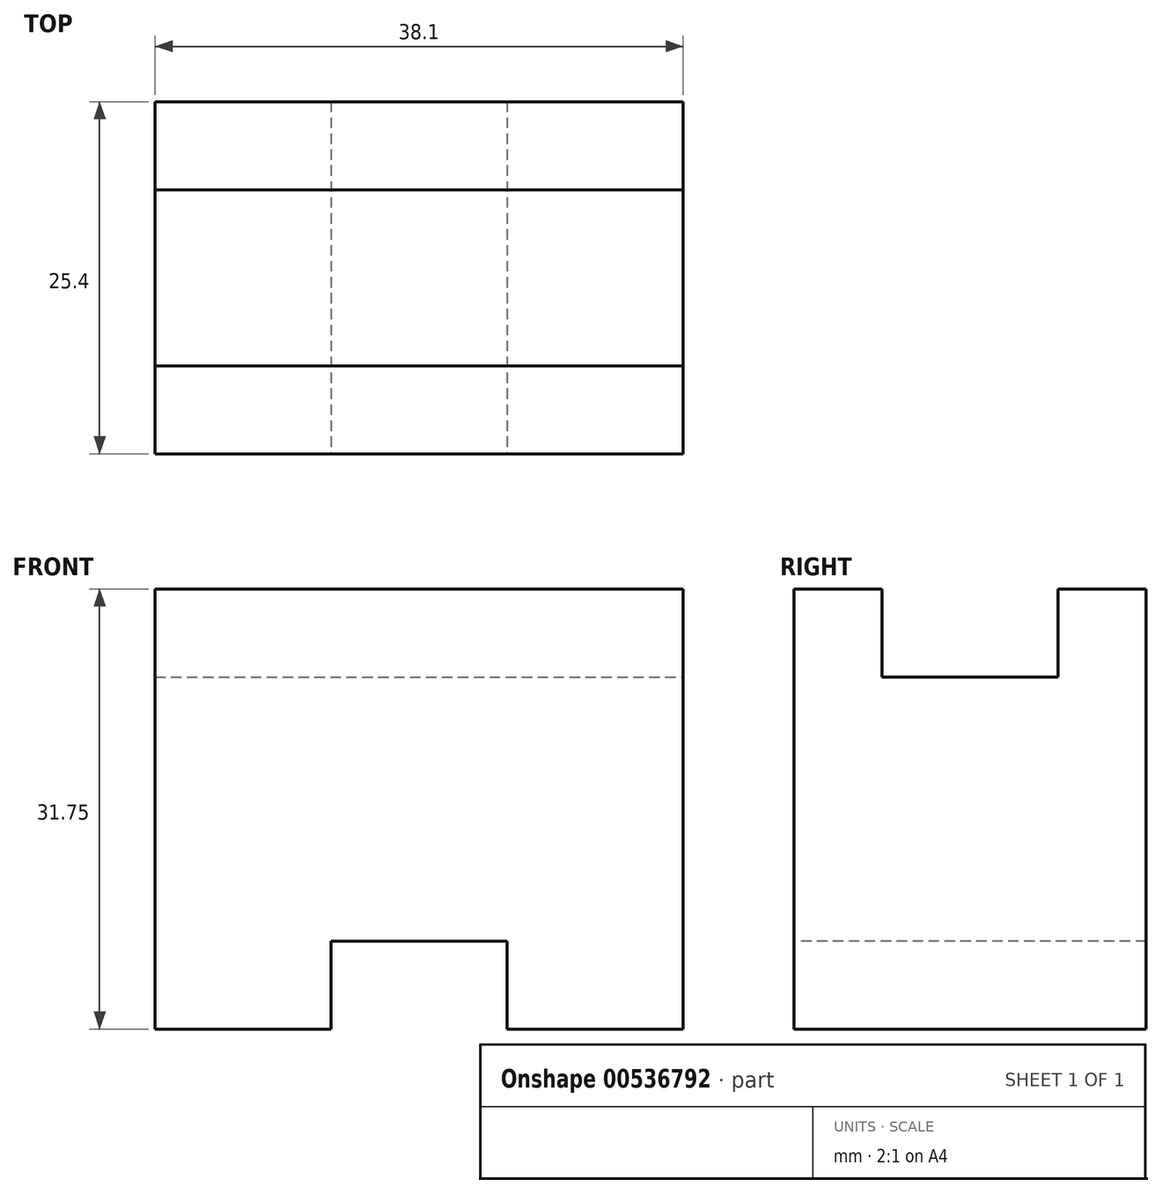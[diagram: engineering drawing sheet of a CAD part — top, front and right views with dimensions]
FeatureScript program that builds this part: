
annotation { "Feature Type Name" : "Feature", "Feature Type Description" : "" }
export const myFeature = defineFeature(function(context is Context, id is Id, definition is map)
    precondition{}
    {
        {
            var Q0;
            Q0=qCreatedBy(makeId("Right.planeOp"),FACE);
            var sketch = newSketch(context, id + "F0", { "sketchPlane" : qUnion([Q0])});
            skLineSegment(sketch, "E0", {"start": v(0, 0) * mm, "end": v(25.4, 0) * mm});
            skLineSegment(sketch, "E1", {"start": v(25.4, 0) * mm, "end": v(25.4, 31.75) * mm});
            skLineSegment(sketch, "E2", {"start": v(25.4, 31.75) * mm, "end": v(0, 31.75) * mm});
            skLineSegment(sketch, "E3", {"start": v(0, 31.75) * mm, "end": v(0, 0) * mm});
            skSolve(sketch);
        }
        {
            var Q0;
            Q0 = qSketchRegion(id + "F0", true);
            extrude(context, id + "F1", {"entities" : qUnion([Q0]), "oppositeDirection" : true, "depth" : 38.1 * mm, "offsetDistance" : 25.4 * mm});
        }
        {
            var Q0;
            Q0=makeQuery(id+"F1.opExtrude","CAP_FACE",FACE,{"disambiguationData":[OSD([sQuery(id+"F0.wireOp",EDGE,"E0"),sQuery(id+"F0.wireOp",EDGE,"E1"),sQuery(id+"F0.wireOp",EDGE,"E2"),sQuery(id+"F0.wireOp",EDGE,"E3")])],"isStart":true});
            var sketch = newSketch(context, id + "F2", { "sketchPlane" : qUnion([Q0])});
            skLineSegment(sketch, "E4", {"start": v(0, 31.75) * mm, "end": v(6.35, 31.75) * mm});
            skLineSegment(sketch, "E5", {"start": v(6.35, 31.75) * mm, "end": v(6.35, 25.4) * mm});
            skLineSegment(sketch, "E6", {"start": v(6.35, 25.4) * mm, "end": v(19.05, 25.4) * mm});
            skLineSegment(sketch, "E7", {"start": v(19.05, 25.4) * mm, "end": v(19.05, 31.75) * mm});
            skSolve(sketch);
        }
        {
            var Q0;
            Q0 = qSketchRegion(id + "F2", true);
            var Q1;
            {var subQ0=sQuery(id+"F2.wireOp",EDGE,"E5");Q1=makeQuery(id+"F2.imprint","IMPRINT",FACE,{"disambiguationData":[TD([[makeQuery(id+"F2.imprint","IMPRINT",EDGE,{"derivedFrom":subQ0}),1.0]])]});}
            extrude(context, id + "F3", {"entities" : qUnion([Q0, Q1]), "operationType" : NewBodyOperationType.REMOVE, "oppositeDirection" : true, "depth" : 38.1 * mm, "offsetDistance" : 25.4 * mm});
        }
        {
            var Q0;
            Q0=makeQuery(id+"F1.opExtrude","SWEPT_FACE",FACE,{"disambiguationData":[OSD([sQuery(id+"F0.wireOp",EDGE,"E3")])]});
            var sketch = newSketch(context, id + "F4", { "sketchPlane" : qUnion([Q0])});
            skLineSegment(sketch, "E8", {"start": v(-38.1, 0) * mm, "end": v(-25.4, 0) * mm});
            skLineSegment(sketch, "E9", {"start": v(-25.4, 0) * mm, "end": v(-25.4, 6.35) * mm});
            skLineSegment(sketch, "E10", {"start": v(-25.4, 6.35) * mm, "end": v(-12.7, 6.35) * mm});
            skLineSegment(sketch, "E11", {"start": v(-12.7, 6.35) * mm, "end": v(-12.7, 0) * mm});
            skSolve(sketch);
        }
        {
            var Q0;
            Q0 = qSketchRegion(id + "F4", true);
            var Q1;
            {var subQ0=sQuery(id+"F4.wireOp",EDGE,"E9");Q1=makeQuery(id+"F4.imprint","IMPRINT",FACE,{"disambiguationData":[TD([[makeQuery(id+"F4.imprint","IMPRINT",EDGE,{"derivedFrom":subQ0}),-1.0]])]});}
            extrude(context, id + "F5", {"entities" : qUnion([Q0, Q1]), "operationType" : NewBodyOperationType.REMOVE, "oppositeDirection" : true, "depth" : 25.4 * mm, "offsetDistance" : 25.4 * mm});
        }
    });
